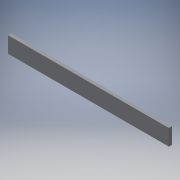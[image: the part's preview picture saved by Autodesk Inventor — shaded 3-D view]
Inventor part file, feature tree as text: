
AUTODESK INVENTOR PART (.ipt)
format: ipt  version: 2019 (Build 230136000, 136)  size: 95,232 bytes
history: native  units: mm
features: extrude x1, sketch x1
ambient origin geometry x8: Origin, YZ Plane, XZ Plane, XY Plane, X Axis, Y Axis, Z Axis, Center Point
bodies: Solid1 (feature_tree)
feature tree (2):
  extrude  "Extrusion1"  Depth=52.0mm
  sketch  "Sketch1"  dims[d0=520.0mm d1=52.0mm d2=10.0mm d3=0.0mm]
